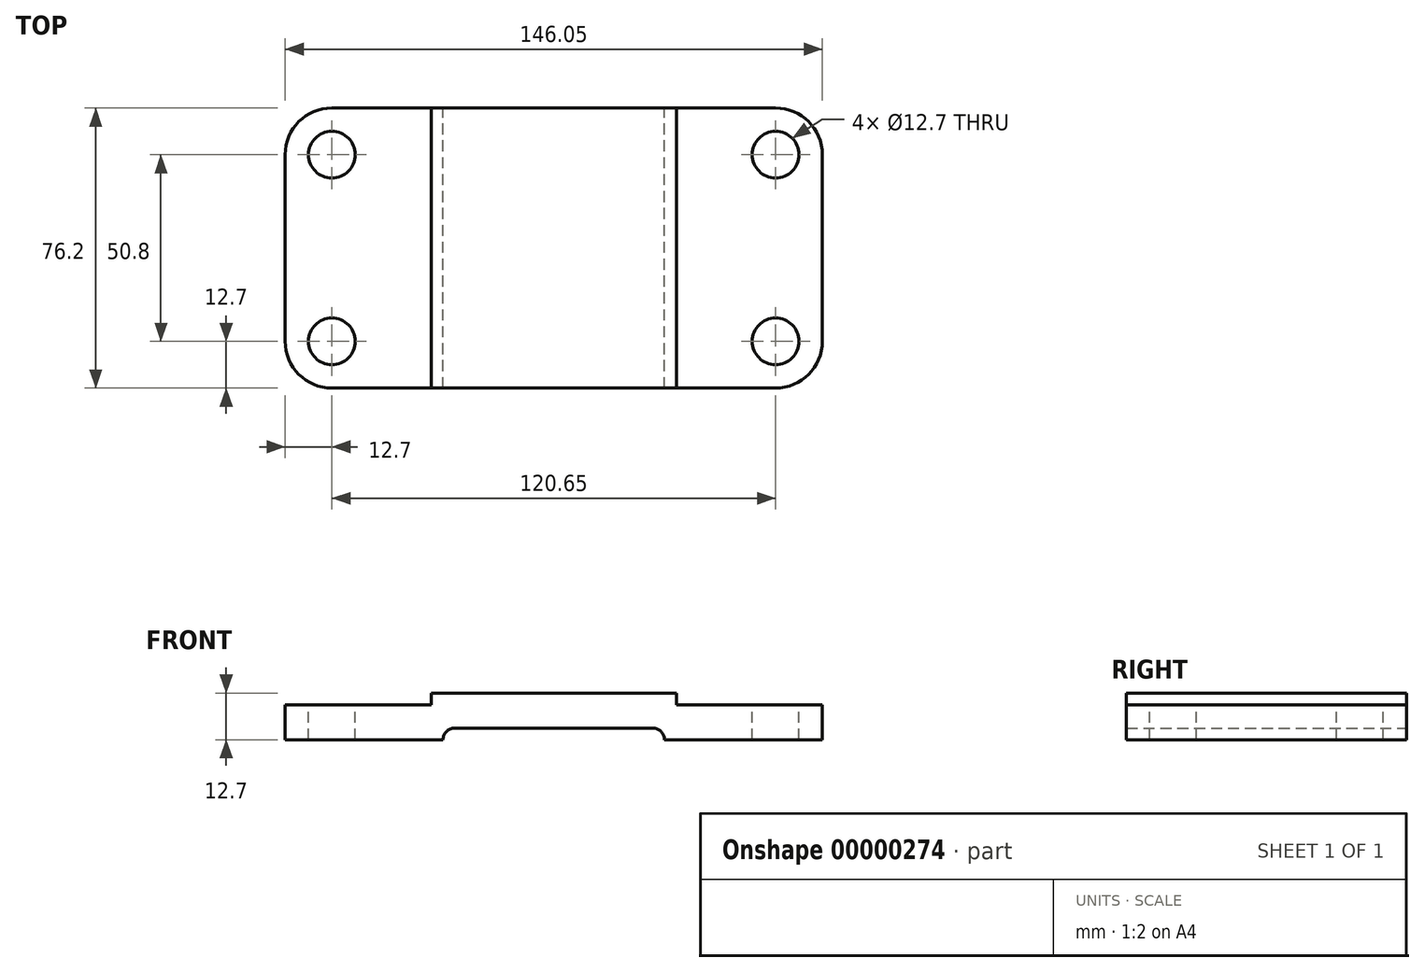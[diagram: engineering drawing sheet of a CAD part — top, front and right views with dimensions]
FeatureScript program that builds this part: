
annotation { "Feature Type Name" : "Feature", "Feature Type Description" : "" }
export const myFeature = defineFeature(function(context is Context, id is Id, definition is map)
    precondition{}
    {
        {
            var Q0;
            Q0=qCreatedBy(makeId("Front.planeOp"),FACE);
            var sketch = newSketch(context, id + "F0", { "sketchPlane" : qUnion([Q0])});
            skLineSegment(sketch, "E0", {"start": v(0, 0) * mm, "end": v(0, 9.53) * mm});
            skLineSegment(sketch, "E1", {"start": v(0, 9.53) * mm, "end": v(39.69, 9.53) * mm});
            skLineSegment(sketch, "E2", {"start": v(39.69, 9.53) * mm, "end": v(39.69, 12.7) * mm});
            skLineSegment(sketch, "E3", {"start": v(39.69, 12.7) * mm, "end": v(106.36, 12.7) * mm});
            skLineSegment(sketch, "E4", {"start": v(106.36, 12.7) * mm, "end": v(106.36, 9.53) * mm});
            skLineSegment(sketch, "E5", {"start": v(106.36, 9.53) * mm, "end": v(146.05, 9.53) * mm});
            skLineSegment(sketch, "E6", {"start": v(146.05, 9.53) * mm, "end": v(146.05, 0) * mm});
            skLineSegment(sketch, "E7", {"start": v(146.05, 0) * mm, "end": v(103.12, 0) * mm});
            skLineSegment(sketch, "E8", {"start": v(103.12, 0) * mm, "end": v(103.12, 3.18) * mm});
            skLineSegment(sketch, "E9", {"start": v(103.12, 3.18) * mm, "end": v(42.93, 3.18) * mm});
            skLineSegment(sketch, "E10", {"start": v(42.93, 3.18) * mm, "end": v(42.93, 0) * mm});
            skLineSegment(sketch, "E11", {"start": v(42.93, 0) * mm, "end": v(0, 0) * mm});
            skSolve(sketch);
        }
        {
            var Q0;
            Q0=makeQuery(id+"F0.imprint","IMPRINT",FACE,{"disambiguationData":[TD([[makeQuery(id+"F0.imprint","IMPRINT",EDGE,{"derivedFrom":sQuery(id+"F0.wireOp",EDGE,"E0")}),-1.0]])]});
            extrude(context, id + "F1", {"entities" : qUnion([Q0]), "depth" : 76.2 * mm});
        }
        {
            var Q0;
            Q0=makeQuery(id+"F1.opExtrude","CAP_EDGE",EDGE,{"disambiguationData":[OSD([sQuery(id+"F0.wireOp",EDGE,"E6")])],"isStart":false});
            var Q1;
            Q1=makeQuery(id+"F1.opExtrude","CAP_EDGE",EDGE,{"disambiguationData":[OSD([sQuery(id+"F0.wireOp",EDGE,"E6")])],"isStart":true});
            var Q2;
            Q2=makeQuery(id+"F1.opExtrude","CAP_EDGE",EDGE,{"disambiguationData":[OSD([sQuery(id+"F0.wireOp",EDGE,"E0")])],"isStart":false});
            var Q3;
            Q3=makeQuery(id+"F1.opExtrude","CAP_EDGE",EDGE,{"disambiguationData":[OSD([sQuery(id+"F0.wireOp",EDGE,"E0")])],"isStart":true});
            fillet(context, id + "F2", {"entities" : qUnion([Q0, Q1, Q2, Q3]), "radius" : 12.7 * mm, "tangentPropagation" : true, "allowEdgeOverflow" : false});
        }
        {
            var Q0;
            Q0=makeQuery(id+"F1.opExtrude","SWEPT_FACE",FACE,{"disambiguationData":[OSD([sQuery(id+"F0.wireOp",EDGE,"E1")])]});
            var sketch = newSketch(context, id + "F3", { "sketchPlane" : qUnion([Q0])});
            skCircle(sketch, "E12", {"center": v(12.7, -12.7) * mm, "radius": 6.35 * mm});
            skCircle(sketch, "E13", {"center": v(12.7, -63.5) * mm, "radius": 6.35 * mm});
            skSolve(sketch);
        }
        {
            var Q0;
            Q0=makeQuery(id+"F1.opExtrude","SWEPT_FACE",FACE,{"disambiguationData":[OSD([sQuery(id+"F0.wireOp",EDGE,"E5")])]});
            var sketch = newSketch(context, id + "F4", { "sketchPlane" : qUnion([Q0])});
            skCircle(sketch, "E14", {"center": v(133.35, -12.7) * mm, "radius": 6.35 * mm});
            skCircle(sketch, "E15", {"center": v(133.35, -63.5) * mm, "radius": 6.35 * mm});
            skSolve(sketch);
        }
        {
            var Q0;
            Q0=makeQuery(id+"F3.imprint","IMPRINT",FACE,{"disambiguationData":[TD([[makeQuery(id+"F3.imprint","IMPRINT",EDGE,{"derivedFrom":sQuery(id+"F3.wireOp",EDGE,"E12")}),1.0]])]});
            var Q1;
            Q1=makeQuery(id+"F3.imprint","IMPRINT",FACE,{"disambiguationData":[TD([[makeQuery(id+"F3.imprint","IMPRINT",EDGE,{"derivedFrom":sQuery(id+"F3.wireOp",EDGE,"E13")}),1.0]])]});
            var Q2;
            Q2=makeQuery(id+"F4.imprint","IMPRINT",FACE,{"disambiguationData":[TD([[makeQuery(id+"F4.imprint","IMPRINT",EDGE,{"derivedFrom":sQuery(id+"F4.wireOp",EDGE,"E14")}),1.0]])]});
            var Q3;
            Q3=makeQuery(id+"F4.imprint","IMPRINT",FACE,{"disambiguationData":[TD([[makeQuery(id+"F4.imprint","IMPRINT",EDGE,{"derivedFrom":sQuery(id+"F4.wireOp",EDGE,"E15")}),1.0]])]});
            extrude(context, id + "F5", {"entities" : qUnion([Q0, Q1, Q2, Q3]), "operationType" : NewBodyOperationType.REMOVE, "endBound" : BoundingType.THROUGH_ALL, "oppositeDirection" : true, "depth" : 25.4 * mm});
        }
        {
            var Q0;
            Q0=makeQuery(id+"F1.opExtrude","SWEPT_EDGE",EDGE,{"disambiguationData":[OSD([sQuery(id+"F0.wireOp",EDGE,"E9"),sQuery(id+"F0.wireOp",EDGE,"E10")])]});
            var Q1;
            Q1=makeQuery(id+"F1.opExtrude","SWEPT_EDGE",EDGE,{"disambiguationData":[OSD([sQuery(id+"F0.wireOp",EDGE,"E8"),sQuery(id+"F0.wireOp",EDGE,"E9")])]});
            fillet(context, id + "F6", {"entities" : qUnion([Q0, Q1]), "radius" : 3.17 * mm, "tangentPropagation" : true, "allowEdgeOverflow" : false});
        }
    });
